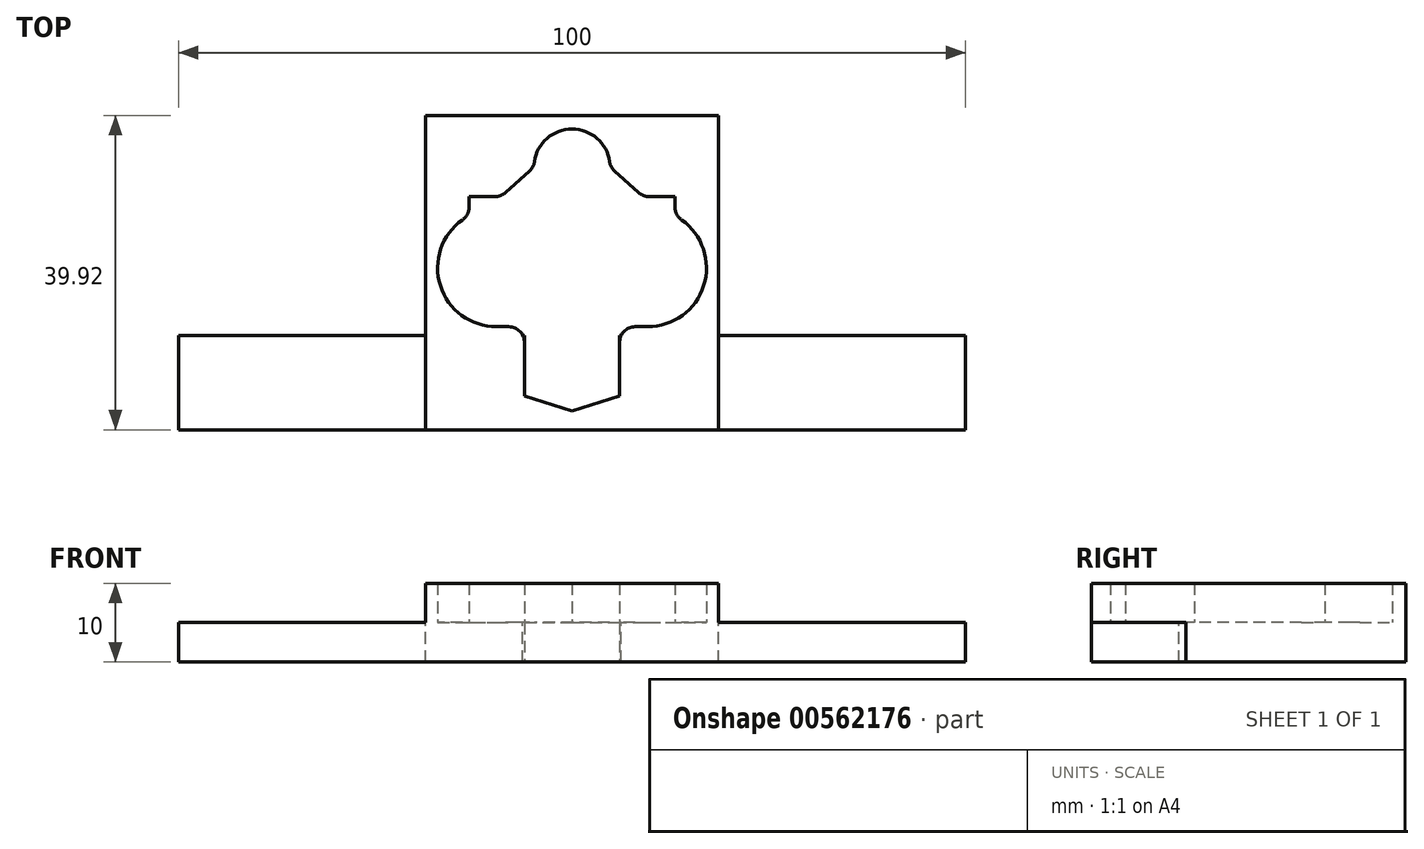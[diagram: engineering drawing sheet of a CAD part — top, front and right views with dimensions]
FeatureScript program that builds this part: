
annotation { "Feature Type Name" : "Feature", "Feature Type Description" : "" }
export const myFeature = defineFeature(function(context is Context, id is Id, definition is map)
    precondition{}
    {
        {
            var Q0;
            Q0=qCreatedBy(makeId("Top.planeOp"),FACE);
            var sketch = newSketch(context, id + "F0", { "sketchPlane" : qUnion([Q0])});
            skLineSegment(sketch, "E0.bottom", {"start": v(0, 0) * mm, "end": v(34.15, 0) * mm});
            skLineSegment(sketch, "E0.top", {"start": v(0, 35.81) * mm, "end": v(34.15, 35.81) * mm});
            skLineSegment(sketch, "E0.left", {"start": v(0, 0) * mm, "end": v(0, 35.8) * mm});
            skLineSegment(sketch, "E0.right", {"start": v(34.15, 0) * mm, "end": v(34.15, 35.8) * mm});
            skCircle(sketch, "E1", {"center": v(7.48, 18.18) * mm, "radius": 7.48 * mm});
            skLineSegment(sketch, "E2", {"start": v(7.48, 18.18) * mm, "end": v(26.67, 18.18) * mm});
            skCircle(sketch, "E3", {"center": v(26.67, 18.18) * mm, "radius": 7.48 * mm});
            skCircle(sketch, "E4", {"center": v(7.48, 18.18) * mm, "radius": 6.03 * mm});
            skCircle(sketch, "E5", {"center": v(26.67, 18.18) * mm, "radius": 6.03 * mm});
            skLineSegment(sketch, "E6.bottom", {"start": v(11.04, 18.18) * mm, "end": v(23.11, 18.18) * mm});
            skLineSegment(sketch, "E6.top", {"start": v(11.04, 0) * mm, "end": v(23.1, 0) * mm});
            skLineSegment(sketch, "E6.left", {"start": v(11.04, 18.18) * mm, "end": v(11.04, 0) * mm});
            skLineSegment(sketch, "E6.right", {"start": v(23.1, 18.18) * mm, "end": v(23.1, 0) * mm});
            skLineSegment(sketch, "E7", {"start": v(17.08, 18.18) * mm, "end": v(17.08, 0) * mm});
            skLineSegment(sketch, "E8", {"start": v(11.04, 1.9) * mm, "end": v(17.07, 0) * mm});
            skLineSegment(sketch, "E9", {"start": v(17.07, 0) * mm, "end": v(23.11, 1.9) * mm});
            skLineSegment(sketch, "E10", {"start": v(7.48, 10.7) * mm, "end": v(26.68, 10.7) * mm});
            skLineSegment(sketch, "E11", {"start": v(7.48, 25.65) * mm, "end": v(26.67, 25.65) * mm});
            skLineSegment(sketch, "E12.bottom", {"start": v(4, 27.23) * mm, "end": v(30.14, 27.23) * mm});
            skLineSegment(sketch, "E12.top", {"start": v(4, 25.65) * mm, "end": v(30.14, 25.65) * mm});
            skLineSegment(sketch, "E12.left", {"start": v(4, 27.23) * mm, "end": v(4, 25.65) * mm});
            skLineSegment(sketch, "E12.right", {"start": v(30.14, 27.23) * mm, "end": v(30.14, 25.65) * mm});
            skLineSegment(sketch, "E13", {"start": v(17.07, 25.65) * mm, "end": v(17.07, 35.81) * mm});
            skLineSegment(sketch, "E14", {"start": v(4, 25.65) * mm, "end": v(4, 24.8) * mm});
            skLineSegment(sketch, "E15", {"start": v(30.14, 25.65) * mm, "end": v(30.14, 24.8) * mm});
            skCircle(sketch, "E16", {"center": v(17.08, 30.99) * mm, "radius": 4.82 * mm});
            skLineSegment(sketch, "E17", {"start": v(17.08, 30.99) * mm, "end": v(12.26, 30.99) * mm});
            skLineSegment(sketch, "E18", {"start": v(12.26, 31) * mm, "end": v(8.07, 27.23) * mm});
            skLineSegment(sketch, "E19", {"start": v(17.08, 30.99) * mm, "end": v(21.9, 30.99) * mm});
            skLineSegment(sketch, "E20", {"start": v(21.9, 30.99) * mm, "end": v(26.07, 27.23) * mm});
            skSolve(sketch);
        }
        {
            var Q0;
            Q0=qCreatedBy(makeId("Top.planeOp"),FACE);
            var sketch = newSketch(context, id + "F1", { "sketchPlane" : qUnion([Q0])});
            skArc(sketch, "E21.0", {"start": v(4, 24.8) * mm, "mid": v(0.22, 16.4) * mm, "end": v(7.48, 10.7) * mm});
            skArc(sketch, "E22.0", {"start": v(26.67, 10.7) * mm, "mid": v(33.93, 16.4) * mm, "end": v(30.14, 24.8) * mm});
            skPoint(sketch, "E23.0", {"position": v(14.06, 0.95) * mm});
            skLineSegment(sketch, "E24.0", {"start": v(11.04, 1.9) * mm, "end": v(17.07, 0) * mm});
            skLineSegment(sketch, "E25.0", {"start": v(17.07, 0) * mm, "end": v(23.11, 1.9) * mm});
            skLineSegment(sketch, "E26.0", {"start": v(12.26, 31) * mm, "end": v(8.07, 27.23) * mm});
            skLineSegment(sketch, "E27.0", {"start": v(21.9, 30.99) * mm, "end": v(26.07, 27.23) * mm});
            skArc(sketch, "E28.0", {"start": v(21.9, 30.99) * mm, "mid": v(17.08, 35.81) * mm, "end": v(12.26, 31) * mm});
            skLineSegment(sketch, "E29", {"start": v(4, 27.23) * mm, "end": v(4, 24.8) * mm});
            skLineSegment(sketch, "E30", {"start": v(30.14, 27.23) * mm, "end": v(30.14, 24.8) * mm});
            skLineSegment(sketch, "E31", {"start": v(7.48, 10.7) * mm, "end": v(11.04, 10.7) * mm});
            skLineSegment(sketch, "E32", {"start": v(11.04, 1.9) * mm, "end": v(11.04, 10.7) * mm});
            skLineSegment(sketch, "E33", {"start": v(23.11, 1.9) * mm, "end": v(23.11, 10.7) * mm});
            skLineSegment(sketch, "E34.trimOffspring", {"start": v(23.11, 10.7) * mm, "end": v(26.67, 10.7) * mm});
            skLineSegment(sketch, "E35.trimOffspring", {"start": v(26.07, 27.23) * mm, "end": v(30.14, 27.23) * mm});
            skLineSegment(sketch, "E36", {"start": v(4, 27.23) * mm, "end": v(8.07, 27.23) * mm});
            skLineSegment(sketch, "E37.bottom", {"start": v(-1.5, 37.53) * mm, "end": v(35.65, 37.53) * mm});
            skLineSegment(sketch, "E37.top", {"start": v(-1.5, -2.4) * mm, "end": v(35.65, -2.4) * mm});
            skLineSegment(sketch, "E37.left", {"start": v(-1.5, 37.53) * mm, "end": v(-1.5, -2.4) * mm});
            skLineSegment(sketch, "E37.right", {"start": v(35.65, 37.53) * mm, "end": v(35.65, -2.4) * mm});
            skSolve(sketch);
        }
        {
            var Q0;
            Q0=makeQuery(id+"F1.imprint","IMPRINT",FACE,{"disambiguationData":[TD([[makeQuery(id+"F1.imprint","IMPRINT",EDGE,{"derivedFrom":sQuery(id+"F1.wireOp",EDGE,"E21.0")}),-1.0]])]});
            extrude(context, id + "F2", {"entities" : qUnion([Q0]), "depth" : 5 * mm, "offsetDistance" : 25 * mm});
        }
        {
            var Q0;
            Q0=makeQuery(id+"F2.opExtrude","SWEPT_EDGE",EDGE,{"disambiguationData":[OSD([sQuery(id+"F1.wireOp",EDGE,"E26.0"),sQuery(id+"F1.wireOp",EDGE,"E36")])]});
            var Q1;
            Q1=makeQuery(id+"F2.opExtrude","SWEPT_EDGE",EDGE,{"disambiguationData":[OSD([sQuery(id+"F1.wireOp",EDGE,"E26.0"),sQuery(id+"F1.wireOp",EDGE,"E28.0")])]});
            var Q2;
            Q2=makeQuery(id+"F2.opExtrude","SWEPT_EDGE",EDGE,{"disambiguationData":[OSD([sQuery(id+"F1.wireOp",EDGE,"E27.0"),sQuery(id+"F1.wireOp",EDGE,"E28.0")])]});
            var Q3;
            Q3=makeQuery(id+"F2.opExtrude","SWEPT_EDGE",EDGE,{"disambiguationData":[OSD([sQuery(id+"F1.wireOp",EDGE,"E27.0"),sQuery(id+"F1.wireOp",EDGE,"E35.trimOffspring")])]});
            var Q4;
            Q4=makeQuery(id+"F2.opExtrude","SWEPT_EDGE",EDGE,{"disambiguationData":[OSD([sQuery(id+"F1.wireOp",EDGE,"E22.0"),sQuery(id+"F1.wireOp",EDGE,"E30")])]});
            var Q5;
            Q5=makeQuery(id+"F2.opExtrude","SWEPT_EDGE",EDGE,{"disambiguationData":[OSD([sQuery(id+"F1.wireOp",EDGE,"E21.0"),sQuery(id+"F1.wireOp",EDGE,"E29")])]});
            var Q6;
            Q6=makeQuery(id+"F2.opExtrude","SWEPT_EDGE",EDGE,{"disambiguationData":[OSD([sQuery(id+"F1.wireOp",EDGE,"E31"),sQuery(id+"F1.wireOp",EDGE,"E32")])]});
            var Q7;
            Q7=makeQuery(id+"F2.opExtrude","SWEPT_EDGE",EDGE,{"disambiguationData":[OSD([sQuery(id+"F1.wireOp",EDGE,"E33"),sQuery(id+"F1.wireOp",EDGE,"E34.trimOffspring")])]});
            fillet(context, id + "F3", {"entities" : qUnion([Q0, Q1, Q2, Q3, Q4, Q5, Q6, Q7]), "radius" : 2 * mm, "tangentPropagation" : true, "allowEdgeOverflow" : false});
        }
        {
            var Q0;
            Q0=makeQuery(id+"F2.opExtrude","CAP_FACE",FACE,{"disambiguationData":[OSD([sQuery(id+"F1.wireOp",EDGE,"E21.0"),sQuery(id+"F1.wireOp",EDGE,"E22.0"),sQuery(id+"F1.wireOp",EDGE,"E24.0"),sQuery(id+"F1.wireOp",EDGE,"E25.0"),sQuery(id+"F1.wireOp",EDGE,"E26.0"),sQuery(id+"F1.wireOp",EDGE,"E27.0"),sQuery(id+"F1.wireOp",EDGE,"E28.0"),sQuery(id+"F1.wireOp",EDGE,"E29"),sQuery(id+"F1.wireOp",EDGE,"E30"),sQuery(id+"F1.wireOp",EDGE,"E31"),sQuery(id+"F1.wireOp",EDGE,"E32"),sQuery(id+"F1.wireOp",EDGE,"E33"),sQuery(id+"F1.wireOp",EDGE,"E34.trimOffspring"),sQuery(id+"F1.wireOp",EDGE,"E35.trimOffspring"),sQuery(id+"F1.wireOp",EDGE,"E36"),sQuery(id+"F1.wireOp",EDGE,"E37.bottom"),sQuery(id+"F1.wireOp",EDGE,"E37.top"),sQuery(id+"F1.wireOp",EDGE,"E37.left"),sQuery(id+"F1.wireOp",EDGE,"E37.right")])],"isStart":true});
            var sketch = newSketch(context, id + "F4", { "sketchPlane" : qUnion([Q0])});
            skLineSegment(sketch, "E38.bottom", {"start": v(67.08, -9.6) * mm, "end": v(-32.92, -9.6) * mm});
            skLineSegment(sketch, "E38.top", {"start": v(67.08, 2.4) * mm, "end": v(-32.92, 2.4) * mm});
            skLineSegment(sketch, "E38.left", {"start": v(67.08, -9.6) * mm, "end": v(67.08, 2.4) * mm});
            skLineSegment(sketch, "E38.right", {"start": v(-32.92, -9.6) * mm, "end": v(-32.92, 2.4) * mm});
            skSolve(sketch);
        }
        {
            var Q0;
            {var subQ0=sQuery(id+"F4.wireOp",EDGE,"E38.right");Q0=makeQuery(id+"F4.imprint","IMPRINT",FACE,{"disambiguationData":[TD([[makeQuery(id+"F4.imprint","IMPRINT",EDGE,{"derivedFrom":subQ0}),-1.0]])]});}
            var Q1;
            {var subQ0=sQuery(id+"F4.wireOp",EDGE,"E38.left");Q1=makeQuery(id+"F4.imprint","IMPRINT",FACE,{"disambiguationData":[TD([[makeQuery(id+"F4.imprint","IMPRINT",EDGE,{"derivedFrom":subQ0}),1.0]])]});}
            var Q2;
            {var subQ8=sQuery(id+"F1.wireOp",EDGE,"E24.0");Q2=makeQuery(id+"F4.imprint","IMPRINT",FACE,{"disambiguationData":[TD([[makeQuery(id+"F4.imprint","IMPRINT",EDGE,{"derivedFrom":makeQuery(id+"F2.opExtrude","CAP_EDGE",EDGE,{"disambiguationData":[OSD([subQ8])],"isStart":true})}),1.0]])]});}
            var Q3;
            {var subQ0=sQuery(id+"F0.wireOp",EDGE,"E8");Q3=makeQuery(id+"F0.imprint","IMPRINT",FACE,{"disambiguationData":[TD([[makeQuery(id+"F0.imprint","IMPRINT",EDGE,{"derivedFrom":subQ0}),1.0]])]});}
            var Q4;
            {var subQ0=sQuery(id+"F0.wireOp",EDGE,"E9");Q4=makeQuery(id+"F0.imprint","IMPRINT",FACE,{"disambiguationData":[TD([[makeQuery(id+"F0.imprint","IMPRINT",EDGE,{"derivedFrom":subQ0}),1.0]])]});}
            extrude(context, id + "F5", {"entities" : qUnion([Q0, Q1, Q2, Q3, Q4]), "operationType" : NewBodyOperationType.ADD, "depth" : 5 * mm, "offsetDistance" : 25 * mm});
        }
        {
            var Q0;
            Q0=makeQuery(id+"F2.opExtrude","CAP_FACE",FACE,{"disambiguationData":[OSD([sQuery(id+"F1.wireOp",EDGE,"E21.0"),sQuery(id+"F1.wireOp",EDGE,"E22.0"),sQuery(id+"F1.wireOp",EDGE,"E24.0"),sQuery(id+"F1.wireOp",EDGE,"E25.0"),sQuery(id+"F1.wireOp",EDGE,"E26.0"),sQuery(id+"F1.wireOp",EDGE,"E27.0"),sQuery(id+"F1.wireOp",EDGE,"E28.0"),sQuery(id+"F1.wireOp",EDGE,"E29"),sQuery(id+"F1.wireOp",EDGE,"E30"),sQuery(id+"F1.wireOp",EDGE,"E31"),sQuery(id+"F1.wireOp",EDGE,"E32"),sQuery(id+"F1.wireOp",EDGE,"E33"),sQuery(id+"F1.wireOp",EDGE,"E34.trimOffspring"),sQuery(id+"F1.wireOp",EDGE,"E35.trimOffspring"),sQuery(id+"F1.wireOp",EDGE,"E36"),sQuery(id+"F1.wireOp",EDGE,"E37.bottom"),sQuery(id+"F1.wireOp",EDGE,"E37.top"),sQuery(id+"F1.wireOp",EDGE,"E37.left"),sQuery(id+"F1.wireOp",EDGE,"E37.right")])],"isStart":true});
            var sketch = newSketch(context, id + "F6", { "sketchPlane" : qUnion([Q0])});
            skLineSegment(sketch, "E39.bottom", {"start": v(35.65, -37.53) * mm, "end": v(-1.5, -37.53) * mm});
            skLineSegment(sketch, "E39.top", {"start": v(35.65, -9.6) * mm, "end": v(-1.5, -9.6) * mm});
            skLineSegment(sketch, "E39.left", {"start": v(35.65, -37.53) * mm, "end": v(35.65, -9.6) * mm});
            skLineSegment(sketch, "E39.right", {"start": v(-1.5, -37.53) * mm, "end": v(-1.5, -9.6) * mm});
            skSolve(sketch);
        }
        {
            var Q0;
            Q0=makeQuery(id+"F6.imprint","IMPRINT",FACE,{"disambiguationData":[TD([[makeQuery(id+"F6.imprint","IMPRINT",EDGE,{"derivedFrom":sQuery(id+"F6.wireOp",EDGE,"E39.bottom")}),1.0]])]});
            var Q1;
            {var subQ1=sQuery(id+"F1.wireOp",EDGE,"E21.0");Q1=makeQuery(id+"F6.imprint","IMPRINT",FACE,{"disambiguationData":[TD([[makeQuery(id+"F6.imprint","IMPRINT",EDGE,{"derivedFrom":makeQuery(id+"F2.opExtrude","CAP_EDGE",EDGE,{"disambiguationData":[OSD([subQ1])],"isStart":true})}),-1.0]])]});}
            extrude(context, id + "F7", {"entities" : qUnion([Q0, Q1]), "operationType" : NewBodyOperationType.ADD, "depth" : 5 * mm, "offsetDistance" : 25 * mm});
        }
    });
